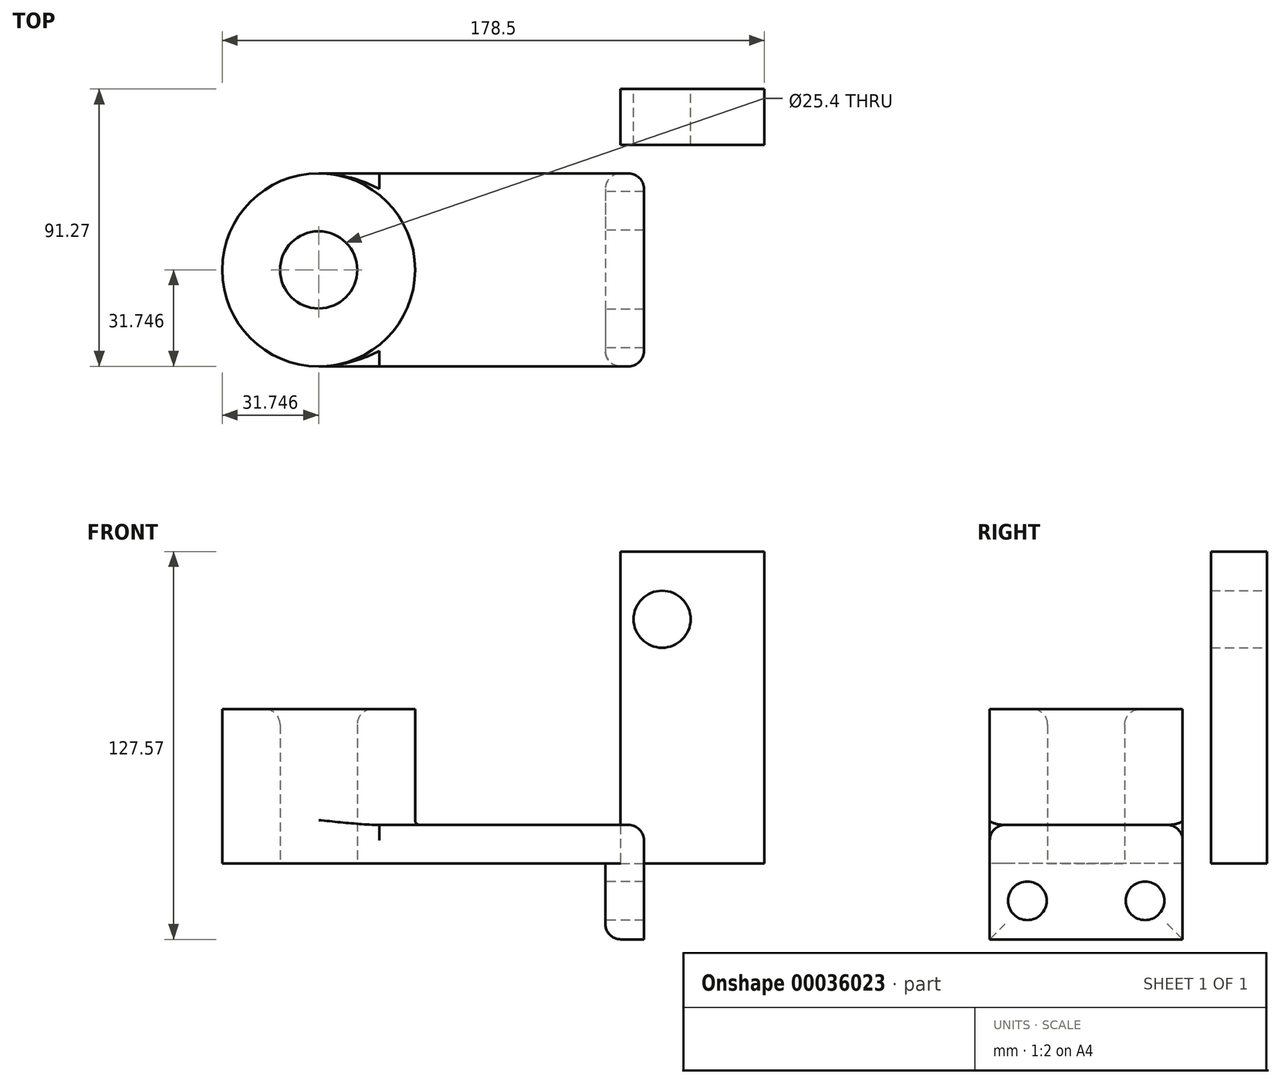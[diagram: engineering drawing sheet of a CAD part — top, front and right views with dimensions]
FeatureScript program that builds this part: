
annotation { "Feature Type Name" : "Feature", "Feature Type Description" : "" }
export const myFeature = defineFeature(function(context is Context, id is Id, definition is map)
    precondition{}
    {
        {
            var Q0;
            Q0=qCreatedBy(makeId("Top.planeOp"),FACE);
            var sketch = newSketch(context, id + "F0", { "sketchPlane" : qUnion([Q0])});
            skLineSegment(sketch, "E0.bottom", {"start": v(-75.35, 31.03) * mm, "end": v(19.04, 31.03) * mm});
            skLineSegment(sketch, "E0.top", {"start": v(-75.35, -32.47) * mm, "end": v(19.04, -32.47) * mm});
            skLineSegment(sketch, "E0.left", {"start": v(-75.35, 31.03) * mm, "end": v(-75.35, -32.47) * mm});
            skLineSegment(sketch, "E0.right", {"start": v(19.04, 31.03) * mm, "end": v(19.04, -32.47) * mm});
            skCircle(sketch, "E1", {"center": v(-75.35, -0.72) * mm, "radius": 31.75 * mm});
            skCircle(sketch, "E2", {"center": v(-75.35, -0.72) * mm, "radius": 12.7 * mm});
            skSolve(sketch);
        }
        {
            var Q0;
            {var subQ3=sQuery(id+"F0.wireOp",EDGE,"E0.bottom");Q0=makeQuery(id+"F0.imprint","IMPRINT",FACE,{"disambiguationData":[TD([[makeQuery(id+"F0.imprint","IMPRINT",EDGE,{"derivedFrom":subQ3}),-1.0]])]});}
            var Q1;
            {var subQ0=sQuery(id+"F0.wireOp",EDGE,"E2");var subQ1=sQuery(id+"F0.wireOp",EDGE,"E0.left");var subQ3=makeQuery(id+"F0.imprint","INTERSECT",VERTEX,{"disambiguationData":[OD(0.0)],"derivedFrom":[subQ1,subQ0]});Q1=makeQuery(id+"F0.imprint","IMPRINT",FACE,{"disambiguationData":[TD([[makeQuery(id+"F0.imprint","IMPRINT",EDGE,{"disambiguationData":[TD([[subQ3,1.0]])],"derivedFrom":subQ0}),-1.0]])]});}
            var Q2;
            {var subQ0=sQuery(id+"F0.wireOp",EDGE,"E2");var subQ1=sQuery(id+"F0.wireOp",EDGE,"E0.left");var subQ3=makeQuery(id+"F0.imprint","INTERSECT",VERTEX,{"disambiguationData":[OD(0.0)],"derivedFrom":[subQ1,subQ0]});Q2=makeQuery(id+"F0.imprint","IMPRINT",FACE,{"disambiguationData":[TD([[makeQuery(id+"F0.imprint","IMPRINT",EDGE,{"disambiguationData":[TD([[subQ3,-1.0]])],"derivedFrom":subQ0}),-1.0]])]});}
            extrude(context, id + "F1", {"entities" : qUnion([Q0, Q1, Q2]), "depth" : 12.7 * mm});
        }
        {
            var Q0;
            {var subQ0=sQuery(id+"F0.wireOp",EDGE,"E2");var subQ1=sQuery(id+"F0.wireOp",EDGE,"E0.left");var subQ3=makeQuery(id+"F0.imprint","INTERSECT",VERTEX,{"disambiguationData":[OD(0.0)],"derivedFrom":[subQ1,subQ0]});Q0=makeQuery(id+"F0.imprint","IMPRINT",FACE,{"disambiguationData":[TD([[makeQuery(id+"F0.imprint","IMPRINT",EDGE,{"disambiguationData":[TD([[subQ3,-1.0]])],"derivedFrom":subQ0}),-1.0]])]});}
            var Q1;
            {var subQ0=sQuery(id+"F0.wireOp",EDGE,"E2");var subQ1=sQuery(id+"F0.wireOp",EDGE,"E0.left");var subQ3=makeQuery(id+"F0.imprint","INTERSECT",VERTEX,{"disambiguationData":[OD(0.0)],"derivedFrom":[subQ1,subQ0]});Q1=makeQuery(id+"F0.imprint","IMPRINT",FACE,{"disambiguationData":[TD([[makeQuery(id+"F0.imprint","IMPRINT",EDGE,{"disambiguationData":[TD([[subQ3,1.0]])],"derivedFrom":subQ0}),-1.0]])]});}
            extrude(context, id + "F2", {"entities" : qUnion([Q0, Q1]), "operationType" : NewBodyOperationType.ADD, "depth" : 50.8 * mm});
        }
        {
            var Q0;
            Q0=makeQuery(id+"F1.opExtrude","SWEPT_FACE",FACE,{"disambiguationData":[OSD([sQuery(id+"F0.wireOp",EDGE,"E0.right")])]});
            var sketch = newSketch(context, id + "F3", { "sketchPlane" : qUnion([Q0])});
            skLineSegment(sketch, "E3.bottom", {"start": v(-32.47, 12.7) * mm, "end": v(31.03, 12.7) * mm});
            skLineSegment(sketch, "E3.top", {"start": v(-32.47, -24.95) * mm, "end": v(31.03, -24.95) * mm});
            skLineSegment(sketch, "E3.left", {"start": v(-32.47, 12.7) * mm, "end": v(-32.47, -24.95) * mm});
            skLineSegment(sketch, "E3.right", {"start": v(31.03, 12.7) * mm, "end": v(31.03, -24.95) * mm});
            skCircle(sketch, "E4", {"center": v(-20.08, -12.25) * mm, "radius": 6.35 * mm});
            skLineSegment(sketch, "E5", {"start": v(-0.72, 12.7) * mm, "end": v(-0.72, -24.95) * mm, "construction": true});
            skCircle(sketch, "E6.MirrorC", {"center": v(18.64, -12.25) * mm, "radius": 6.35 * mm});
            skSolve(sketch);
        }
        {
            var Q0;
            {var subQ2=sQuery(id+"F3.wireOp",EDGE,"E3.top");Q0=makeQuery(id+"F3.imprint","IMPRINT",FACE,{"disambiguationData":[TD([[makeQuery(id+"F3.imprint","IMPRINT",EDGE,{"derivedFrom":subQ2}),1.0]])]});}
            var Q1;
            {var subQ2=sQuery(id+"F3.wireOp",EDGE,"E3.bottom");Q1=makeQuery(id+"F3.imprint","IMPRINT",FACE,{"disambiguationData":[TD([[makeQuery(id+"F3.imprint","IMPRINT",EDGE,{"derivedFrom":subQ2}),1.0]])]});}
            extrude(context, id + "F4", {"entities" : qUnion([Q0, Q1]), "operationType" : NewBodyOperationType.ADD, "depth" : 12.7 * mm});
        }
        {
            var Q0;
            {var subQ0=sQuery(id+"F0.wireOp",EDGE,"E1");Q0=makeQuery(id+"F2.boolean.opBoolean","INTERSECT",EDGE,{"derivedFrom":[makeQuery(id+"F1.opExtrude","CAP_FACE",FACE,{"disambiguationData":[OSD([sQuery(id+"F0.wireOp",EDGE,"E0.bottom"),sQuery(id+"F0.wireOp",EDGE,"E0.top"),sQuery(id+"F0.wireOp",EDGE,"E0.right"),subQ0,sQuery(id+"F0.wireOp",EDGE,"E2")])],"isStart":false}),makeQuery(id+"F2.opExtrude","SWEPT_FACE",FACE,{"disambiguationData":[OSD([subQ0])]})]});}
            fillet(context, id + "F5", {"entities" : qUnion([Q0]), "radius" : 1.59 * mm, "tangentPropagation" : true, "allowEdgeOverflow" : false});
        }
        {
            var Q0;
            Q0=makeQuery(id+"F4.opExtrude","CAP_EDGE",EDGE,{"disambiguationData":[OSD([sQuery(id+"F3.wireOp",EDGE,"E3.bottom")])],"isStart":false});
            fillet(context, id + "F6", {"entities" : qUnion([Q0]), "radius" : 5.08 * mm, "tangentPropagation" : true, "allowEdgeOverflow" : false});
        }
        {
            var Q0;
            Q0=makeQuery(id+"F4.boolean.opBoolean","MERGE",EDGE,{"derivedFrom":[makeQuery(id+"F1.opExtrude","CAP_EDGE",EDGE,{"disambiguationData":[OSD([sQuery(id+"F0.wireOp",EDGE,"E0.top")])],"isStart":false}),makeQuery(id+"F4.opExtrude","SWEPT_EDGE",EDGE,{"disambiguationData":[OSD([sQuery(id+"F3.wireOp",EDGE,"E3.bottom"),sQuery(id+"F3.wireOp",EDGE,"E3.left")])]})]});
            var Q1;
            Q1=makeQuery(id+"F4.opExtrude","CAP_EDGE",EDGE,{"disambiguationData":[OSD([sQuery(id+"F3.wireOp",EDGE,"E3.left")])],"isStart":false});
            var Q2;
            Q2=makeQuery(id+"F4.opExtrude","CAP_EDGE",EDGE,{"disambiguationData":[OSD([sQuery(id+"F3.wireOp",EDGE,"E3.right")])],"isStart":false});
            var Q3;
            Q3=makeQuery(id+"F4.boolean.opBoolean","MERGE",EDGE,{"derivedFrom":[makeQuery(id+"F1.opExtrude","CAP_EDGE",EDGE,{"disambiguationData":[OSD([sQuery(id+"F0.wireOp",EDGE,"E0.bottom")])],"isStart":false}),makeQuery(id+"F4.opExtrude","SWEPT_EDGE",EDGE,{"disambiguationData":[OSD([sQuery(id+"F3.wireOp",EDGE,"E3.bottom"),sQuery(id+"F3.wireOp",EDGE,"E3.right")])]})]});
            var Q4;
            Q4=makeQuery(id+"F2.opExtrude","CAP_EDGE",EDGE,{"disambiguationData":[OSD([sQuery(id+"F0.wireOp",EDGE,"E2")])],"isStart":false});
            fillet(context, id + "F7", {"entities" : qUnion([Q0, Q1, Q2, Q3, Q4]), "radius" : 5.08 * mm, "tangentPropagation" : true, "allowEdgeOverflow" : false});
        }
        {
            var Q0;
            Q0=makeQuery(id+"F4.opExtrude","CAP_EDGE",EDGE,{"disambiguationData":[OSD([sQuery(id+"F3.wireOp",EDGE,"E3.right")])],"isStart":true});
            var Q1;
            Q1=makeQuery(id+"F4.opExtrude","CAP_EDGE",EDGE,{"disambiguationData":[OSD([sQuery(id+"F3.wireOp",EDGE,"E3.left")])],"isStart":true});
            var Q2;
            Q2=makeQuery(id+"F4.opExtrude","CAP_EDGE",EDGE,{"disambiguationData":[OSD([sQuery(id+"F3.wireOp",EDGE,"E3.top")])],"isStart":true});
            fillet(context, id + "F8", {"entities" : qUnion([Q0, Q1, Q2]), "radius" : 5.08 * mm, "tangentPropagation" : true, "allowEdgeOverflow" : false});
        }
        {
            var Q0;
            Q0=qCreatedBy(makeId("Top.planeOp"),FACE);
            var sketch = newSketch(context, id + "F9", { "sketchPlane" : qUnion([Q0])});
            skLineSegment(sketch, "E7.bottom", {"start": v(24.03, 58.8) * mm, "end": v(71.4, 58.8) * mm});
            skLineSegment(sketch, "E7.top", {"start": v(24.03, 40.4) * mm, "end": v(71.4, 40.4) * mm});
            skLineSegment(sketch, "E7.left", {"start": v(24.03, 58.8) * mm, "end": v(24.03, 40.4) * mm});
            skLineSegment(sketch, "E7.right", {"start": v(71.4, 58.8) * mm, "end": v(71.4, 40.4) * mm});
            skSolve(sketch);
        }
        {
            var Q0;
            Q0=makeQuery(id+"F9.imprint","IMPRINT",FACE,{"disambiguationData":[TD([[makeQuery(id+"F9.imprint","IMPRINT",EDGE,{"derivedFrom":sQuery(id+"F9.wireOp",EDGE,"E7.bottom")}),-1.0]])]});
            extrude(context, id + "F10", {"entities" : qUnion([Q0]), "depth" : 102.62 * mm, "offsetDistance" : 25.4 * mm});
        }
        {
            var Q0;
            Q0=makeQuery(id+"F10.opExtrude","SWEPT_FACE",FACE,{"disambiguationData":[OSD([sQuery(id+"F9.wireOp",EDGE,"E7.bottom")])]});
            var sketch = newSketch(context, id + "F11", { "sketchPlane" : qUnion([Q0])});
            skCircle(sketch, "E8", {"center": v(-37.73, 80.4) * mm, "radius": 9.39 * mm});
            skSolve(sketch);
        }
        {
            var Q0;
            Q0=makeQuery(id+"F11.imprint","IMPRINT",FACE,{"disambiguationData":[TD([[makeQuery(id+"F11.imprint","IMPRINT",EDGE,{"derivedFrom":sQuery(id+"F11.wireOp",EDGE,"E8")}),1.0]])]});
            extrude(context, id + "F12", {"entities" : qUnion([Q0]), "operationType" : NewBodyOperationType.REMOVE, "oppositeDirection" : true, "depth" : 39.37 * mm, "offsetDistance" : 25.4 * mm});
        }
    });
